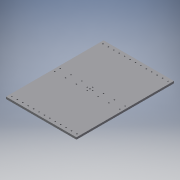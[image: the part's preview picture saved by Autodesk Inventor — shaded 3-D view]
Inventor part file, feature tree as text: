
AUTODESK INVENTOR PART (.ipt)
format: ipt  version: 2016 (Build 200138000, 138)  size: 254,464 bytes
history: native  units: mm
features: reference x100, extrude x1, sketch x1
ambient origin geometry x8: Origin, YZ Plane, XZ Plane, XY Plane, X Axis, Y Axis, Z Axis, Center Point
bodies: Body1 (feature_tree)
feature tree (102):
  extrude  "Extrusion4"  Depth=6.0mm
  sketch  "Sketch1"  dims[d0=208.0mm d1=288.0mm d4=3.7mm d9=6.0mm d10=0.0mm]
  reference  "Reference2"
  reference  "Reference4"
  reference  "Reference6"
  reference  "Reference8"
  reference  "Reference9"
  reference  "Reference10"
  reference  "Reference11"
  reference  "Reference12"
  reference  "Reference13"
  reference  "Reference14"
  reference  "Reference15"
  reference  "Reference16"
  reference  "Reference17"
  reference  "Reference18"
  reference  "Reference19"
  reference  "Reference20"
  reference  "Reference21"
  reference  "Reference22"
  reference  "Reference23"
  reference  "Reference24"
  reference  "Reference25"
  reference  "Reference26"
  reference  "Reference27"
  reference  "Reference28"
  reference  "Reference29"
  reference  "Reference30"
  reference  "Reference31"
  reference  "Reference32"
  reference  "Reference33"
  reference  "Reference34"
  reference  "Reference35"
  reference  "Reference36"
  reference  "Reference37"
  reference  "Reference38"
  reference  "Reference39"
  reference  "Reference40"
  reference  "Reference41"
  reference  "Reference42"
  reference  "Reference43"
  reference  "Reference44"
  reference  "Reference45"
  reference  "Reference46"
  reference  "Reference47"
  reference  "Reference48"
  reference  "Reference49"
  reference  "Reference50"
  reference  "Reference51"
  reference  "Reference52"
  reference  "Reference53"
  reference  "Reference54"
  reference  "Reference55"
  reference  "Reference56"
  reference  "Reference57"
  reference  "Reference58"
  reference  "Reference59"
  reference  "Reference60"
  reference  "Reference61"
  reference  "Reference62"
  reference  "Reference63"
  reference  "Reference64"
  reference  "Reference65"
  reference  "Reference66"
  reference  "Reference67"
  reference  "Reference68"
  reference  "Reference69"
  reference  "Reference70"
  reference  "Reference71"
  reference  "Reference72"
  reference  "Reference73"
  reference  "Reference74"
  reference  "Reference75"
  reference  "Reference76"
  reference  "Reference77"
  reference  "Reference78"
  reference  "Reference79"
  reference  "Reference80"
  reference  "Reference81"
  reference  "Reference82"
  reference  "Reference83"
  reference  "Reference84"
  reference  "Reference85"
  reference  "Reference86"
  reference  "Reference87"
  reference  "Reference88"
  reference  "Reference89"
  reference  "Reference90"
  reference  "Reference91"
  reference  "Reference92"
  reference  "Reference93"
  reference  "Reference94"
  reference  "Reference95"
  reference  "Reference96"
  reference  "Reference97"
  reference  "Reference98"
  reference  "Reference99"
  reference  "Reference100"
  reference  "Reference101"
  reference  "Reference102"
  reference  "Reference103"
  reference  "Reference104"
